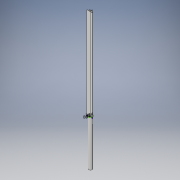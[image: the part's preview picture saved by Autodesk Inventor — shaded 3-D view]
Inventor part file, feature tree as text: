
AUTODESK INVENTOR PART (.ipt)
format: ipt  version: 2019 (Build 230136000, 136)  size: 147,968 bytes
history: native  units: mm
features: extrude x2, sketch x1
ambient origin geometry x8: Origin, YZ Plane, XZ Plane, XY Plane, X Axis, Y Axis, Z Axis, Center Point
bodies: Solid1 (feature_tree)
feature tree (3):
  sketch  "Sketch1"  dims[d0=60.0mm d1=60.0mm d2=5.0mm d3=4.0mm d4=30.0mm d5=4.0mm d6=25.0mm d7=2000.0mm d8=0.0mm d9=80.0mm d10=3.0mm d11=1000.0mm d12=0.0mm]
  extrude  "Extrusion1"  Depth=60.0mm
  extrude  "Extrusion2"  Depth=5.0mm
